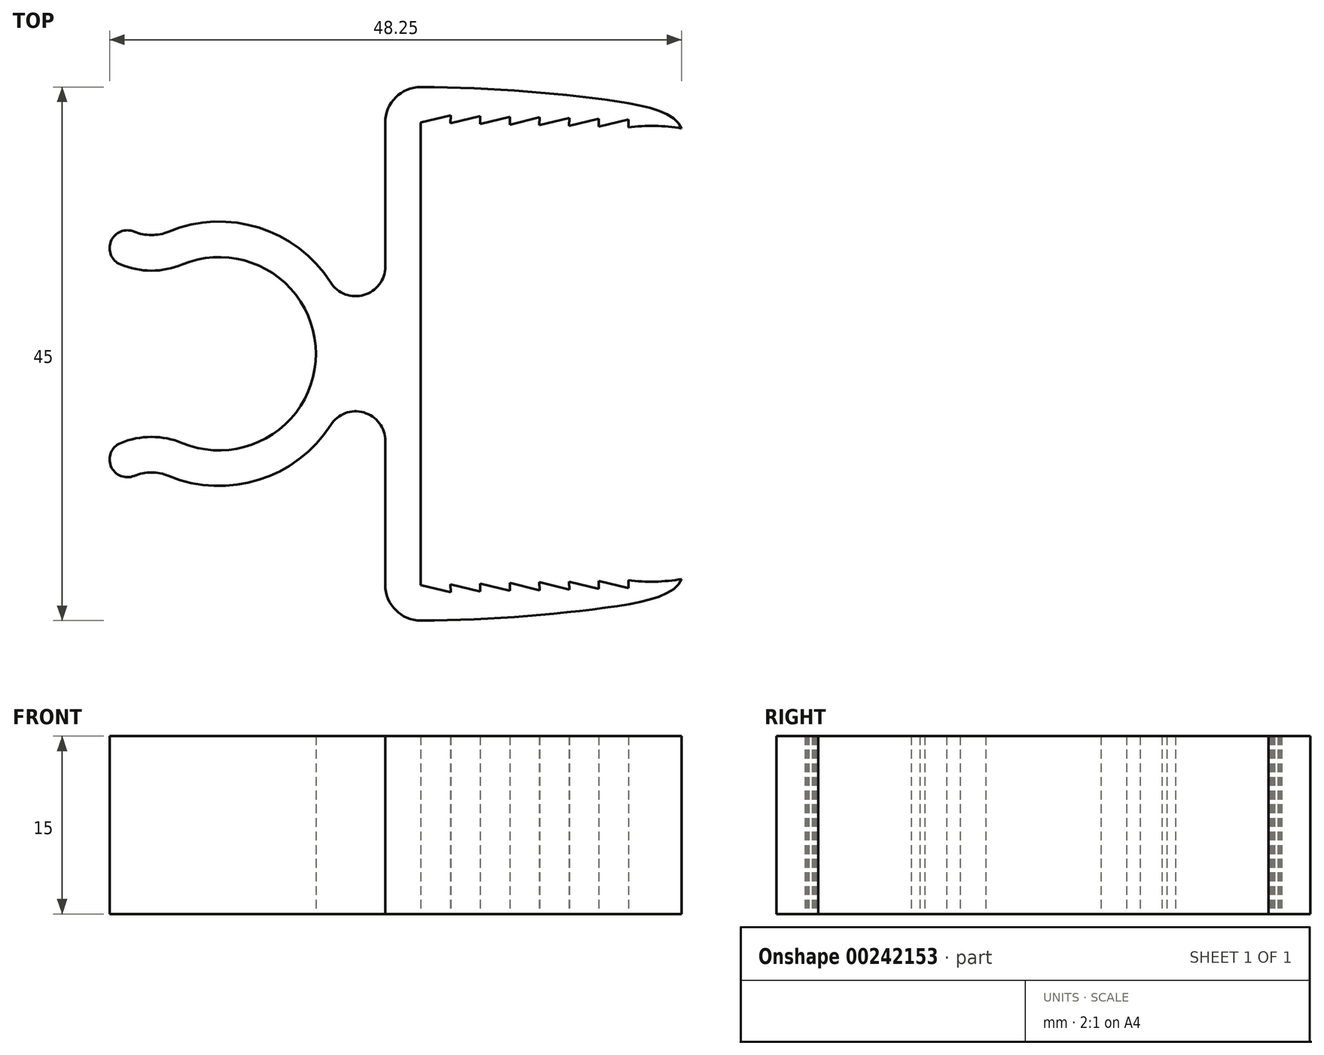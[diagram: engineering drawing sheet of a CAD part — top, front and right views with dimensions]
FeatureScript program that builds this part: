
annotation { "Feature Type Name" : "Feature", "Feature Type Description" : "" }
export const myFeature = defineFeature(function(context is Context, id is Id, definition is map)
    precondition{}
    {
        {
            var Q0;
            Q0=qCreatedBy(makeId("Top.planeOp"),FACE);
            var sketch = newSketch(context, id + "F0", { "sketchPlane" : qUnion([Q0])});
            skLineSegment(sketch, "E0", {"start": v(0, 0) * mm, "end": v(0, 0) * mm});
            skPoint(sketch, "E1", {"position": v(0, 0) * mm});
            skLineSegment(sketch, "E2", {"start": v(-14, 0) * mm, "end": v(-14, 0) * mm});
            skArc(sketch, "E3", {"start": v(-17.12, -7.53) * mm, "mid": v(-5.85, 0) * mm, "end": v(-17.12, 7.53) * mm});
            skArc(sketch, "E4", {"start": v(-18.27, -10.3) * mm, "mid": v(-2.85, 0) * mm, "end": v(-18.27, 10.3) * mm});
            skArc(sketch, "E5", {"start": v(-4.6, 6) * mm, "mid": v(-1.8, 4.95) * mm, "end": v(0, 7.35) * mm});
            skLineSegment(sketch, "E6", {"start": v(-14, 0) * mm, "end": v(0, 0) * mm, "construction": true});
            skArc(sketch, "E7.MirrorCS", {"start": v(-4.6, -6) * mm, "mid": v(-1.8, -4.95) * mm, "end": v(0, -7.35) * mm});
            skLineSegment(sketch, "E8", {"start": v(-14, 0) * mm, "end": v(-18.27, 10.3) * mm, "construction": true});
            skLineSegment(sketch, "E9.MirrorCS", {"start": v(-14, 0) * mm, "end": v(-18.27, -10.3) * mm, "construction": true});
            skPoint(sketch, "E10", {"position": v(-5.85, 0) * mm});
            skPoint(sketch, "E11", {"position": v(-2.85, 0) * mm});
            skArc(sketch, "E12", {"start": v(-21.18, 10.3) * mm, "mid": v(-19.72, 10.01) * mm, "end": v(-18.27, 10.3) * mm});
            skArc(sketch, "E13", {"start": v(-22.32, 7.53) * mm, "mid": v(-19.72, 7.01) * mm, "end": v(-17.12, 7.53) * mm});
            skArc(sketch, "E14", {"start": v(-21.18, 10.3) * mm, "mid": v(-23.14, 9.49) * mm, "end": v(-22.32, 7.53) * mm});
            skArc(sketch, "E15.MirrorCS", {"start": v(-22.32, -7.53) * mm, "mid": v(-19.72, -7.01) * mm, "end": v(-17.12, -7.53) * mm});
            skArc(sketch, "E16.MirrorCS", {"start": v(-21.18, -10.3) * mm, "mid": v(-23.14, -9.49) * mm, "end": v(-22.32, -7.53) * mm});
            skArc(sketch, "E17.MirrorCS", {"start": v(-21.18, -10.3) * mm, "mid": v(-19.72, -10.01) * mm, "end": v(-18.27, -10.3) * mm});
            skLineSegment(sketch, "E18", {"start": v(0, 7.35) * mm, "end": v(0, -7.35) * mm});
            skLineSegment(sketch, "E19", {"start": v(0, 19.5) * mm, "end": v(0, -19.5) * mm});
            skLineSegment(sketch, "E20", {"start": v(3, 19.5) * mm, "end": v(3, -19.5) * mm});
            skPoint(sketch, "E21", {"position": v(3, 0) * mm});
            skLineSegment(sketch, "E22", {"start": v(3, 22.5) * mm, "end": v(3, 22.5) * mm});
            skPoint(sketch, "E23.visualSharp", {"position": v(0, 22.5) * mm});
            skArc(sketch, "E23.filletArc", {"start": v(3, 22.5) * mm, "mid": v(0.88, 21.62) * mm, "end": v(0, 19.5) * mm});
            skFitSpline(sketch, "E24", {"points": [v(3, 22.5) * mm, v(18, 21.5) * mm, v(25, 19) * mm], "startDerivative": vector(25.55, 0) * mm, "endDerivative": vector(4.36, -11.26) * mm});
            skLineSegment(sketch, "E25", {"start": v(3, 19.5) * mm, "end": v(25, 19) * mm, "construction": true});
            skLineSegment(sketch, "E26", {"start": v(3, 19.5) * mm, "end": v(5.51, 20.11) * mm});
            skLineSegment(sketch, "E27", {"start": v(5.51, 20.11) * mm, "end": v(5.5, 19.44) * mm});
            skLineSegment(sketch, "E28.1.0.0", {"start": v(5.5, 19.44) * mm, "end": v(8.01, 20.06) * mm});
            skLineSegment(sketch, "E28.1.0.1", {"start": v(8.01, 20.06) * mm, "end": v(8, 19.39) * mm});
            skLineSegment(sketch, "E28.2.0.0", {"start": v(8, 19.39) * mm, "end": v(10.51, 20) * mm});
            skLineSegment(sketch, "E28.2.0.1", {"start": v(10.51, 20) * mm, "end": v(10.5, 19.33) * mm});
            skLineSegment(sketch, "E28.3.0.0", {"start": v(10.5, 19.33) * mm, "end": v(13.01, 19.94) * mm});
            skLineSegment(sketch, "E28.3.0.1", {"start": v(13.01, 19.94) * mm, "end": v(13, 19.27) * mm});
            skLineSegment(sketch, "E28.4.0.0", {"start": v(13, 19.27) * mm, "end": v(15.51, 19.89) * mm});
            skLineSegment(sketch, "E28.4.0.1", {"start": v(15.51, 19.89) * mm, "end": v(15.5, 19.22) * mm});
            skLineSegment(sketch, "E28.5.0.0", {"start": v(15.5, 19.22) * mm, "end": v(18.01, 19.83) * mm});
            skLineSegment(sketch, "E28.5.0.1", {"start": v(18.01, 19.83) * mm, "end": v(18, 19.16) * mm});
            skLineSegment(sketch, "E28.6.0.0", {"start": v(18, 19.16) * mm, "end": v(20.51, 19.77) * mm});
            skLineSegment(sketch, "E28.6.0.1", {"start": v(20.51, 19.77) * mm, "end": v(20.5, 19.1) * mm});
            skLineSegment(sketch, "E28.direction1", {"start": v(3, 19.5) * mm, "end": v(5.5, 19.44) * mm, "construction": true});
            skLineSegment(sketch, "E29", {"start": v(0, 0) * mm, "end": v(3, 0) * mm});
            skLineSegment(sketch, "E30.MirrorCS", {"start": v(13.01, -19.94) * mm, "end": v(13, -19.27) * mm});
            skLineSegment(sketch, "E31.MirrorCS", {"start": v(20.51, -19.77) * mm, "end": v(20.5, -19.1) * mm});
            skLineSegment(sketch, "E32.MirrorCS", {"start": v(15.51, -19.89) * mm, "end": v(15.5, -19.22) * mm});
            skLineSegment(sketch, "E33.MirrorCS", {"start": v(5.51, -20.11) * mm, "end": v(5.5, -19.44) * mm});
            skLineSegment(sketch, "E34.MirrorCS", {"start": v(18.01, -19.83) * mm, "end": v(18, -19.16) * mm});
            skLineSegment(sketch, "E35.MirrorCS", {"start": v(8.01, -20.06) * mm, "end": v(8, -19.39) * mm});
            skLineSegment(sketch, "E36.MirrorCS", {"start": v(10.51, -20) * mm, "end": v(10.5, -19.33) * mm});
            skLineSegment(sketch, "E37.MirrorCS", {"start": v(3, -19.5) * mm, "end": v(5.5, -19.44) * mm, "construction": true});
            skLineSegment(sketch, "E38.MirrorCS", {"start": v(3, -22.5) * mm, "end": v(3, -22.5) * mm});
            skLineSegment(sketch, "E39.MirrorCS", {"start": v(3, -19.5) * mm, "end": v(25, -19) * mm, "construction": true});
            skLineSegment(sketch, "E40.MirrorCS", {"start": v(13, -19.27) * mm, "end": v(15.51, -19.89) * mm});
            skLineSegment(sketch, "E41.MirrorCS", {"start": v(8, -19.39) * mm, "end": v(10.51, -20) * mm});
            skFitSpline(sketch, "E42.MirrorCS", {"points": [v(3, -22.5) * mm, v(18, -21.5) * mm, v(25, -19) * mm], "startDerivative": vector(25.55, 0) * mm, "endDerivative": vector(4.36, 11.26) * mm});
            skLineSegment(sketch, "E43.MirrorCS", {"start": v(15.5, -19.22) * mm, "end": v(18.01, -19.83) * mm});
            skLineSegment(sketch, "E44.MirrorCS", {"start": v(10.5, -19.33) * mm, "end": v(13.01, -19.94) * mm});
            skLineSegment(sketch, "E45.MirrorCS", {"start": v(5.5, -19.44) * mm, "end": v(8.01, -20.06) * mm});
            skPoint(sketch, "E46.MirrorP", {"position": v(0, -22.5) * mm});
            skLineSegment(sketch, "E47.MirrorCS", {"start": v(3, -19.5) * mm, "end": v(5.51, -20.11) * mm});
            skLineSegment(sketch, "E48.MirrorCS", {"start": v(18, -19.16) * mm, "end": v(20.51, -19.77) * mm});
            skArc(sketch, "E49.MirrorCS", {"start": v(3, -22.5) * mm, "mid": v(0.88, -21.62) * mm, "end": v(0, -19.5) * mm});
            skArc(sketch, "E50", {"start": v(25, 19) * mm, "mid": v(22.75, 19.22) * mm, "end": v(20.5, 19.1) * mm});
            skArc(sketch, "E51.MirrorCS", {"start": v(25, -19) * mm, "mid": v(22.75, -19.22) * mm, "end": v(20.5, -19.1) * mm});
            skSolve(sketch);
        }
        {
            var Q0;
            Q0=makeQuery(id+"F0.imprint","IMPRINT",FACE,{"disambiguationData":[TD([[makeQuery(id+"F0.imprint","IMPRINT",EDGE,{"derivedFrom":sQuery(id+"F0.wireOp",EDGE,"E3")}),-1.0]])]});
            var Q1;
            {var subQ1=sQuery(id+"F0.wireOp",EDGE,"E5");Q1=makeQuery(id+"F0.imprint","IMPRINT",FACE,{"disambiguationData":[TD([[makeQuery(id+"F0.imprint","IMPRINT",EDGE,{"derivedFrom":subQ1}),-1.0]])]});}
            var Q2;
            {var subQ1=sQuery(id+"F0.wireOp",EDGE,"E23.filletArc");Q2=makeQuery(id+"F0.imprint","IMPRINT",FACE,{"disambiguationData":[TD([[makeQuery(id+"F0.imprint","IMPRINT",EDGE,{"derivedFrom":subQ1}),1.0]])]});}
            var Q3;
            {var subQ1=sQuery(id+"F0.wireOp",EDGE,"E29");Q3=makeQuery(id+"F0.imprint","IMPRINT",FACE,{"disambiguationData":[TD([[makeQuery(id+"F0.imprint","IMPRINT",EDGE,{"derivedFrom":subQ1}),-1.0]])]});}
            extrude(context, id + "F1", {"entities" : qUnion([Q0, Q1, Q2, Q3]), "depth" : 15 * mm});
        }
    });
